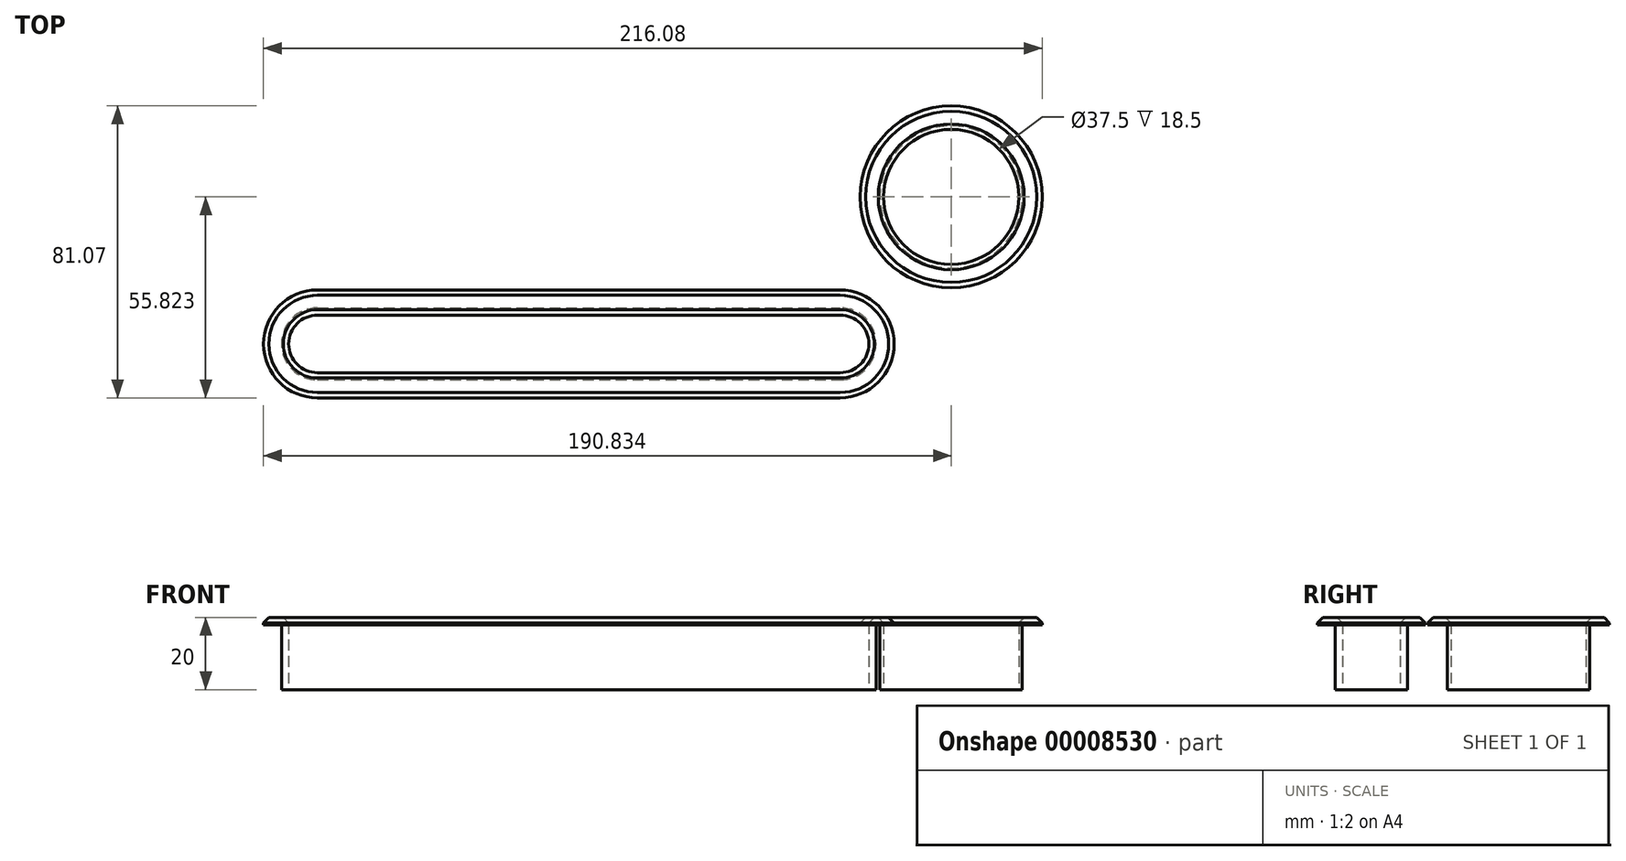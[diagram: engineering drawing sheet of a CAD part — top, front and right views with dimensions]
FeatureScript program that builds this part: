
annotation { "Feature Type Name" : "Feature", "Feature Type Description" : "" }
export const myFeature = defineFeature(function(context is Context, id is Id, definition is map)
    precondition{}
    {
        {
            var Q0;
            Q0=qCreatedBy(makeId("Top.planeOp"),FACE);
            var sketch = newSketch(context, id + "F0", { "sketchPlane" : qUnion([Q0])});
            skArc(sketch, "E0", {"start": v(0, -10) * mm, "mid": v(10, 0) * mm, "end": v(0, 10) * mm});
            skArc(sketch, "E1", {"start": v(-145, 10) * mm, "mid": v(-155, 0) * mm, "end": v(-145, -10) * mm});
            skLineSegment(sketch, "E2", {"start": v(-145, 10) * mm, "end": v(0, 10) * mm});
            skLineSegment(sketch, "E3", {"start": v(-145, -10) * mm, "end": v(0, -10) * mm});
            skLineSegment(sketch, "E4.0", {"start": v(-145, 8) * mm, "end": v(0, 8) * mm});
            skArc(sketch, "E4.1", {"start": v(-145, 8) * mm, "mid": v(-153, 0) * mm, "end": v(-145, -8) * mm});
            skLineSegment(sketch, "E4.2", {"start": v(-145, -8) * mm, "end": v(0, -8) * mm});
            skArc(sketch, "E4.3", {"start": v(0, -8) * mm, "mid": v(8, 0) * mm, "end": v(0, 8) * mm});
            skLineSegment(sketch, "E5.0", {"start": v(-145, 15) * mm, "end": v(0, 15) * mm});
            skArc(sketch, "E5.1", {"start": v(-145, 15) * mm, "mid": v(-160, 0) * mm, "end": v(-145, -15) * mm});
            skLineSegment(sketch, "E5.2", {"start": v(-145, -15) * mm, "end": v(0, -15) * mm});
            skArc(sketch, "E5.3", {"start": v(0, -15) * mm, "mid": v(15, 0) * mm, "end": v(0, 15) * mm});
            skCircle(sketch, "E6", {"center": v(30.83, 40.82) * mm, "radius": 19.75 * mm});
            skCircle(sketch, "E7", {"center": v(30.83, 40.82) * mm, "radius": 18.75 * mm});
            skCircle(sketch, "E8", {"center": v(30.83, 40.82) * mm, "radius": 25.25 * mm});
            skSolve(sketch);
        }
        {
            var Q0;
            Q0=makeQuery(id+"F0.imprint","IMPRINT",FACE,{"disambiguationData":[TD([[makeQuery(id+"F0.imprint","IMPRINT",EDGE,{"derivedFrom":sQuery(id+"F0.wireOp",EDGE,"E0")}),-1.0]])]});
            var Q1;
            Q1=makeQuery(id+"F0.imprint","IMPRINT",FACE,{"disambiguationData":[TD([[makeQuery(id+"F0.imprint","IMPRINT",EDGE,{"derivedFrom":sQuery(id+"F0.wireOp",EDGE,"E0")}),1.0]])]});
            extrude(context, id + "F1", {"entities" : qUnion([Q0, Q1]), "depth" : 2 * mm, "offsetDistance" : 25 * mm});
        }
        {
            var Q0;
            Q0=makeQuery(id+"F0.imprint","IMPRINT",FACE,{"disambiguationData":[TD([[makeQuery(id+"F0.imprint","IMPRINT",EDGE,{"derivedFrom":sQuery(id+"F0.wireOp",EDGE,"E0")}),1.0]])]});
            extrude(context, id + "F2", {"entities" : qUnion([Q0]), "operationType" : NewBodyOperationType.ADD, "oppositeDirection" : true, "depth" : 18 * mm, "offsetDistance" : 25 * mm});
        }
        {
            var Q0;
            Q0=makeQuery(id+"F0.imprint","IMPRINT",FACE,{"disambiguationData":[TD([[makeQuery(id+"F0.imprint","IMPRINT",EDGE,{"derivedFrom":sQuery(id+"F0.wireOp",EDGE,"E6")}),-1.0]])]});
            var Q1;
            Q1=makeQuery(id+"F0.imprint","IMPRINT",FACE,{"disambiguationData":[TD([[makeQuery(id+"F0.imprint","IMPRINT",EDGE,{"derivedFrom":sQuery(id+"F0.wireOp",EDGE,"E6")}),1.0]])]});
            extrude(context, id + "F3", {"entities" : qUnion([Q0, Q1]), "depth" : 2 * mm, "offsetDistance" : 25 * mm});
        }
        {
            var Q0;
            Q0=makeQuery(id+"F0.imprint","IMPRINT",FACE,{"disambiguationData":[TD([[makeQuery(id+"F0.imprint","IMPRINT",EDGE,{"derivedFrom":sQuery(id+"F0.wireOp",EDGE,"E6")}),1.0]])]});
            extrude(context, id + "F4", {"entities" : qUnion([Q0]), "operationType" : NewBodyOperationType.ADD, "oppositeDirection" : true, "depth" : 18 * mm, "offsetDistance" : 25 * mm});
        }
        {
            var Q0;
            Q0=makeQuery(id+"F1.opExtrude","CAP_EDGE",EDGE,{"disambiguationData":[OSD([sQuery(id+"F0.wireOp",EDGE,"E4.1")])],"isStart":false});
            var Q1;
            Q1=makeQuery(id+"F1.opExtrude","CAP_EDGE",EDGE,{"disambiguationData":[OSD([sQuery(id+"F0.wireOp",EDGE,"E5.1")])],"isStart":false});
            var Q2;
            Q2=makeQuery(id+"F1.opExtrude","CAP_EDGE",EDGE,{"disambiguationData":[OSD([sQuery(id+"F0.wireOp",EDGE,"E4.2")])],"isStart":false});
            var Q3;
            Q3=makeQuery(id+"F1.opExtrude","CAP_EDGE",EDGE,{"disambiguationData":[OSD([sQuery(id+"F0.wireOp",EDGE,"E5.2")])],"isStart":false});
            var Q4;
            Q4=makeQuery(id+"F3.opExtrude","CAP_EDGE",EDGE,{"disambiguationData":[OSD([sQuery(id+"F0.wireOp",EDGE,"E8")])],"isStart":false});
            var Q5;
            Q5=makeQuery(id+"F3.opExtrude","CAP_EDGE",EDGE,{"disambiguationData":[OSD([sQuery(id+"F0.wireOp",EDGE,"E7")])],"isStart":false});
            chamfer(context, id + "F5", {"entities" : qUnion([Q0, Q1, Q2, Q3, Q4, Q5]), "width" : 1.5 * mm, "tangentPropagation" : true});
        }
    });
